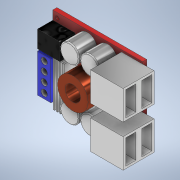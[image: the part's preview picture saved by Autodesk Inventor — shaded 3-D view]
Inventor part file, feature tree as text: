
AUTODESK INVENTOR PART (.ipt)
format: ipt  version: 2021 (Build 250183000, 183)  size: 349,184 bytes
history: native  units: mm
features: extrude x11, sketch x5, mirror x1, fillet x1
ambient origin geometry x8: Origin, YZ Plane, XZ Plane, XY Plane, X Axis, Y Axis, Z Axis, Center Point
bodies: Volumenkörper1 (feature_tree)
feature tree (18):
  sketch  "Skizze1"  dims[d0=39.0mm d1=47.0mm]
  extrude  "Extrusion1"  Depth=47.0mm
  extrude  "Extrusion2"  Depth=2.0mm
  extrude  "Extrusion3"  Depth=6.0mm
  extrude  "Extrusion4"  Depth=10.0mm
  mirror  "Spiegeln1"
  extrude  "Extrusion5"  Depth=1.0mm
  extrude  "Extrusion6"  Depth=16.0mm
  extrude  "Extrusion11"  Depth=15.2mm
  extrude  "Extrusion7"  Depth=6.0mm
  extrude  "Extrusion8"  Depth=17.0mm
  fillet  "Rundung1"  Radius=15.2mm
  extrude  "Extrusion9"  Depth=1.0mm
  extrude  "Extrusion10"  Depth=8.0mm
  sketch  "Skizze2"  dims[d2=3.0mm d3=2.0mm]
  sketch  "Skizze3"  dims[d4=38.3mm d5=6.0mm]
  sketch  "Skizze4"  dims[d6=45.0deg d7=10.0mm]
  sketch  "Skizze5"  dims[d8=0.5mm d9=1.0mm d10=16.0mm d11=15.2mm d13=6.0mm d14=17.0mm d15=15.2mm d16=1.0mm d17=8.0mm d18=20.0mm d19=7.0mm d20=0.1mm d21=5.8mm d22=0.1mm d23=1.0mm d24=1.0mm d25=0.1mm d26=9.0mm d27=1.0mm d28=1.5mm d29=2.2mm d30=0.0mm d31=16.2mm d32=0.0mm d33=1.1mm d34=5.3mm d35=5.3mm d36=3.1mm d37=12.8mm d38=10.0mm d39=0.0mm d40=9.5mm d41=0.0mm d42=13.0mm d43=0.0mm d44=8.0mm d45=0.0mm d46=7.0mm d47=0.0mm d48=5.8mm d49=0.828571mm d50=0.828571mm d51=0.828571mm d52=7.0mm d53=0.0mm d54=0.5mm d55=3.2mm d56=4.8mm d57=4.8mm d58=4.8mm d59=7.0mm d60=0.0mm d61=0.5mm d62=4.5mm d63=3.9mm d64=7.0mm d65=0.0mm d66=5.0mm d67=8.0mm d68=0.0mm]
